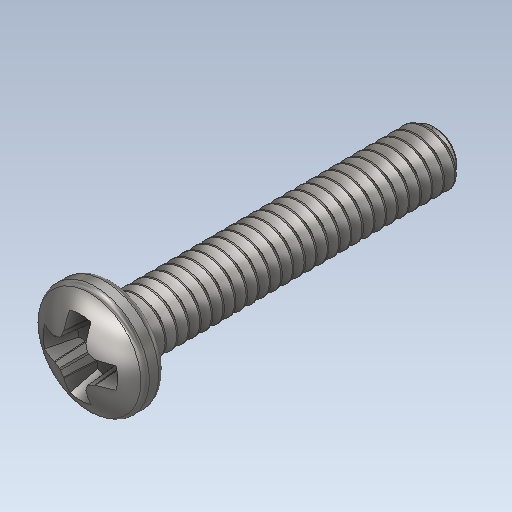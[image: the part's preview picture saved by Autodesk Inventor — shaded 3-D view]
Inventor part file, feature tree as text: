
AUTODESK INVENTOR PART (.ipt)
format: ipt  version: 2020 (Build 240168000, 168)  size: 1,040,384 bytes
history: native  units: in
note: dims shown in document units (in); Inventor stores cm internally (conversion verified against a paired STEP export)
features: fillet x1
ambient origin geometry x8: Origin, YZ Plane, XZ Plane, XY Plane, X Axis, Y Axis, Z Axis, Center Point
bodies: Solid1 (feature_tree)
feature tree (1):
  fillet  "Fillet1"  [1 undecoded]
note: 1 required parameter value undecoded (feature->parameter linkage not recoverable at this tier; creation-order binding heuristic only, values carry confidence <= 0.55)
